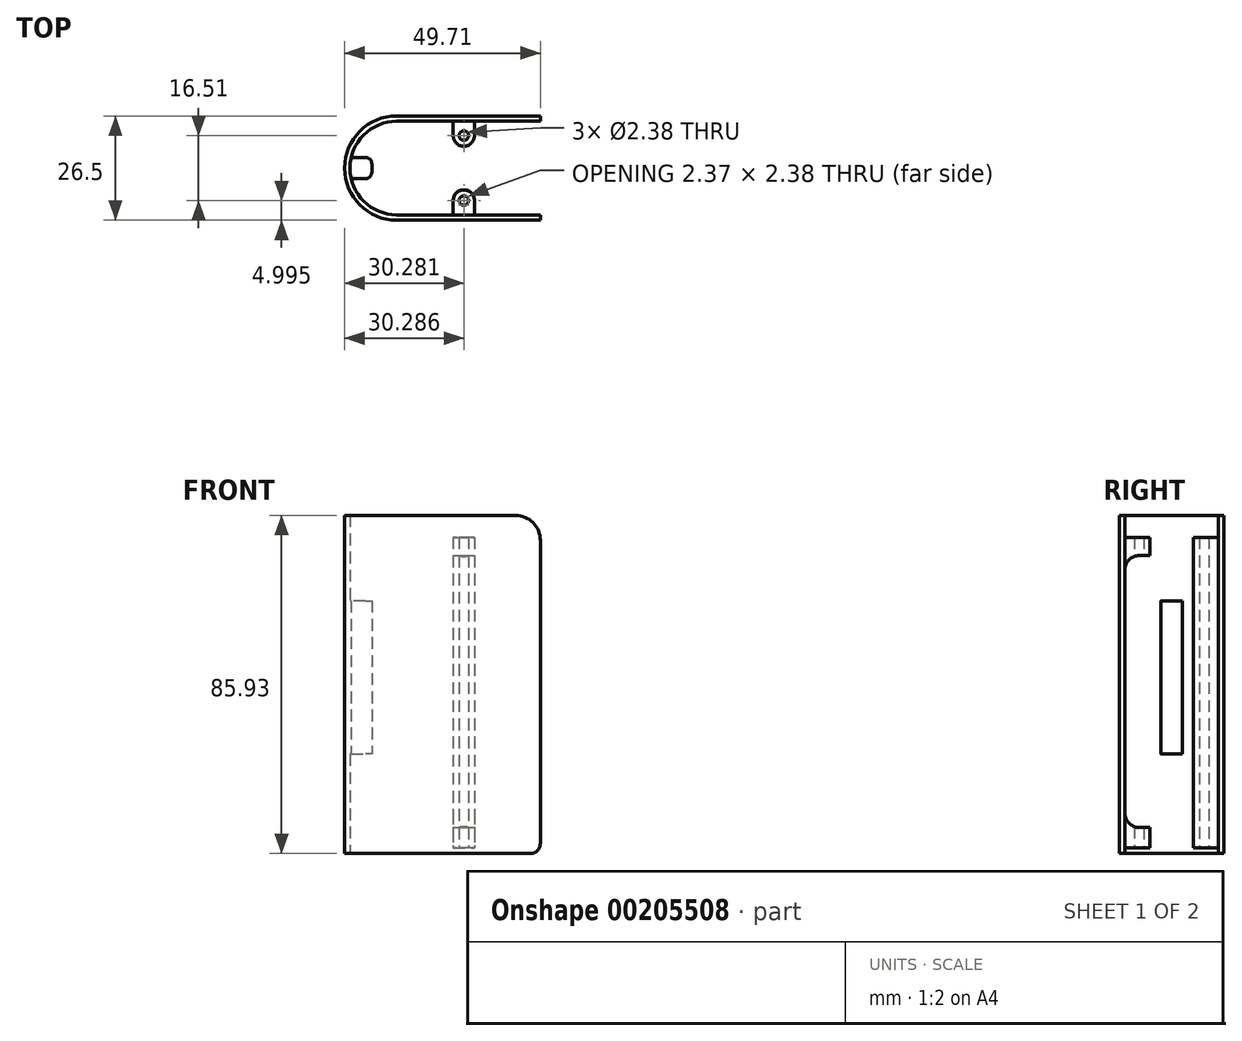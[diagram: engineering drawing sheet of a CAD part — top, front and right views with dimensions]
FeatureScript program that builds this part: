
annotation { "Feature Type Name" : "Feature", "Feature Type Description" : "" }
export const myFeature = defineFeature(function(context is Context, id is Id, definition is map)
    precondition{}
    {
        {
            var Q0;
            Q0=qCreatedBy(makeId("Top.planeOp"),FACE);
            var sketch = newSketch(context, id + "F0", { "sketchPlane" : qUnion([Q0])});
            skArc(sketch, "E0", {"start": v(0, 13.25) * mm, "mid": v(-9.37, 9.37) * mm, "end": v(-13.25, 0) * mm});
            skLineSegment(sketch, "E1", {"start": v(36.46, 13.25) * mm, "end": v(0, 13.25) * mm});
            skLineSegment(sketch, "E2", {"start": v(36.46, 11.9) * mm, "end": v(19.74, 11.9) * mm});
            skArc(sketch, "E3", {"start": v(0, 11.9) * mm, "mid": v(-7.4, 9.32) * mm, "end": v(-11.59, 2.7) * mm});
            skLineSegment(sketch, "E4.trimOffspring", {"start": v(36.46, 11.9) * mm, "end": v(36.46, 13.25) * mm});
            skLineSegment(sketch, "E5", {"start": v(14.33, 8.25) * mm, "end": v(14.33, 11.9) * mm});
            skLineSegment(sketch, "E6.trimOffspring", {"start": v(14.33, 11.9) * mm, "end": v(0, 11.9) * mm});
            skArc(sketch, "E7", {"start": v(14.33, 8.25) * mm, "mid": v(17.03, 5.55) * mm, "end": v(19.74, 8.25) * mm});
            skLineSegment(sketch, "E8.trimOffspring", {"start": v(19.74, 8.25) * mm, "end": v(19.74, 11.9) * mm});
            skCircle(sketch, "E9", {"center": v(17.03, 8.25) * mm, "radius": 1.2 * mm});
            skArc(sketch, "E10.MirrorCS", {"start": v(0, -11.9) * mm, "mid": v(-7.4, -9.32) * mm, "end": v(-11.59, -2.7) * mm});
            skArc(sketch, "E11.MirrorCS", {"start": v(0, -13.25) * mm, "mid": v(-9.37, -9.37) * mm, "end": v(-13.25, 0) * mm});
            skLineSegment(sketch, "E12.MirrorCS", {"start": v(14.33, -11.9) * mm, "end": v(0, -11.9) * mm});
            skLineSegment(sketch, "E13.MirrorCS", {"start": v(36.46, -13.25) * mm, "end": v(0, -13.25) * mm});
            skLineSegment(sketch, "E14.MirrorCS", {"start": v(14.33, -8.25) * mm, "end": v(14.33, -11.9) * mm});
            skArc(sketch, "E15.MirrorCS", {"start": v(14.33, -8.25) * mm, "mid": v(17.03, -5.55) * mm, "end": v(19.74, -8.25) * mm});
            skCircle(sketch, "E16.MirrorC", {"center": v(17.03, -8.25) * mm, "radius": 1.2 * mm});
            skLineSegment(sketch, "E17.MirrorCS", {"start": v(19.74, -8.25) * mm, "end": v(19.74, -11.9) * mm});
            skLineSegment(sketch, "E18.MirrorCS", {"start": v(36.46, -11.9) * mm, "end": v(19.74, -11.9) * mm});
            skLineSegment(sketch, "E19.MirrorCS", {"start": v(36.46, -11.9) * mm, "end": v(36.46, -13.25) * mm});
            skLineSegment(sketch, "E20.bottom", {"start": v(-7.99, 2.7) * mm, "end": v(-11.59, 2.7) * mm});
            skLineSegment(sketch, "E20.top", {"start": v(-7.99, -2.7) * mm, "end": v(-11.59, -2.7) * mm});
            skLineSegment(sketch, "E20.left", {"start": v(-6.34, 1.05) * mm, "end": v(-6.34, -1.05) * mm});
            skPoint(sketch, "E20.middle", {"position": v(-11.9, 0) * mm});
            skPoint(sketch, "E21.visualSharp", {"position": v(-6.34, 2.7) * mm});
            skArc(sketch, "E21.filletArc", {"start": v(-6.34, 1.05) * mm, "mid": v(-6.82, 2.22) * mm, "end": v(-7.99, 2.7) * mm});
            skPoint(sketch, "E22.visualSharp", {"position": v(-6.34, -2.7) * mm});
            skArc(sketch, "E22.filletArc", {"start": v(-7.99, -2.7) * mm, "mid": v(-6.82, -2.22) * mm, "end": v(-6.34, -1.05) * mm});
            skSolve(sketch);
        }
        {
            var Q0;
            Q0 = qSketchRegion(id + "F0", true);
            extrude(context, id + "F1", {"entities" : qUnion([Q0]), "depth" : 85.93 * mm});
        }
        {
            var Q0;
            Q0=makeQuery(id+"F1.opExtrude","CAP_FACE",FACE,{"disambiguationData":[OSD([sQuery(id+"F0.wireOp",EDGE,"E0"),sQuery(id+"F0.wireOp",EDGE,"E1"),sQuery(id+"F0.wireOp",EDGE,"E2"),sQuery(id+"F0.wireOp",EDGE,"E3"),sQuery(id+"F0.wireOp",EDGE,"E4.trimOffspring"),sQuery(id+"F0.wireOp",EDGE,"E5"),sQuery(id+"F0.wireOp",EDGE,"E6.trimOffspring"),sQuery(id+"F0.wireOp",EDGE,"E7"),sQuery(id+"F0.wireOp",EDGE,"E8.trimOffspring"),sQuery(id+"F0.wireOp",EDGE,"E9"),sQuery(id+"F0.wireOp",EDGE,"E10.MirrorCS"),sQuery(id+"F0.wireOp",EDGE,"E11.MirrorCS"),sQuery(id+"F0.wireOp",EDGE,"E12.MirrorCS"),sQuery(id+"F0.wireOp",EDGE,"E13.MirrorCS"),sQuery(id+"F0.wireOp",EDGE,"E14.MirrorCS"),sQuery(id+"F0.wireOp",EDGE,"E15.MirrorCS"),sQuery(id+"F0.wireOp",EDGE,"E16.MirrorC"),sQuery(id+"F0.wireOp",EDGE,"E17.MirrorCS"),sQuery(id+"F0.wireOp",EDGE,"E18.MirrorCS"),sQuery(id+"F0.wireOp",EDGE,"E19.MirrorCS"),sQuery(id+"F0.wireOp",EDGE,"E20.bottom"),sQuery(id+"F0.wireOp",EDGE,"E20.top"),sQuery(id+"F0.wireOp",EDGE,"E20.left"),sQuery(id+"F0.wireOp",EDGE,"E21.filletArc"),sQuery(id+"F0.wireOp",EDGE,"E22.filletArc")])],"isStart":false});
            var sketch = newSketch(context, id + "F2", { "sketchPlane" : qUnion([Q0])});
            skCircle(sketch, "E23", {"center": v(0, 0) * mm, "radius": 11.9 * mm});
            skLineSegment(sketch, "E24.bottom", {"start": v(14.33, 11.9) * mm, "end": v(19.74, 11.9) * mm});
            skLineSegment(sketch, "E24.top", {"start": v(14.33, -11.9) * mm, "end": v(19.74, -11.9) * mm});
            skLineSegment(sketch, "E24.left", {"start": v(14.33, 11.9) * mm, "end": v(14.33, -11.9) * mm});
            skLineSegment(sketch, "E24.right", {"start": v(19.74, 11.9) * mm, "end": v(19.74, -11.9) * mm});
            skSolve(sketch);
        }
        {
            var Q0;
            {var subQ2=makeQuery(id+"F1.opExtrude","CAP_EDGE",EDGE,{"disambiguationData":[OSD([sQuery(id+"F0.wireOp",EDGE,"E20.bottom")])],"isStart":false});Q0=makeQuery(id+"F2.imprint","IMPRINT",FACE,{"disambiguationData":[TD([[makeQuery(id+"F2.imprint","IMPRINT",EDGE,{"derivedFrom":subQ2}),1.0]])]});}
            extrude(context, id + "F3", {"entities" : qUnion([Q0]), "operationType" : NewBodyOperationType.REMOVE, "oppositeDirection" : true, "depth" : 21.72 * mm});
        }
        {
            var Q0;
            Q0 = qSketchRegion(id + "F2", true);
            extrude(context, id + "F4", {"entities" : qUnion([Q0]), "operationType" : NewBodyOperationType.REMOVE, "oppositeDirection" : true, "depth" : 5.6 * mm});
        }
        {
            var Q0;
            Q0=makeQuery(id+"F1.opExtrude","SWEPT_FACE",FACE,{"disambiguationData":[OSD([sQuery(id+"F0.wireOp",EDGE,"E17.MirrorCS")])]});
            var sketch = newSketch(context, id + "F5", { "sketchPlane" : qUnion([Q0])});
            skLineSegment(sketch, "E25", {"start": v(-11.9, 80.34) * mm, "end": v(-11.9, 75.77) * mm});
            skLineSegment(sketch, "E26", {"start": v(-8.25, 0) * mm, "end": v(-8.25, 6.6) * mm});
            skLineSegment(sketch, "E27.bottom", {"start": v(-8.25, 75.77) * mm, "end": v(-8.09, 75.77) * mm});
            skLineSegment(sketch, "E27.top", {"start": v(-8.25, 6.6) * mm, "end": v(-8.09, 6.6) * mm});
            skLineSegment(sketch, "E27.left", {"start": v(-11.9, 71.96) * mm, "end": v(-11.9, 10.41) * mm});
            skLineSegment(sketch, "E28.bottom", {"start": v(-8.25, 6.6) * mm, "end": v(-4.6, 6.6) * mm});
            skLineSegment(sketch, "E28.top", {"start": v(-8.25, 75.77) * mm, "end": v(-4.6, 75.77) * mm});
            skLineSegment(sketch, "E28.right", {"start": v(-4.6, 6.6) * mm, "end": v(-4.6, 75.77) * mm});
            skPoint(sketch, "E29.visualSharp", {"position": v(-11.9, 75.77) * mm});
            skArc(sketch, "E29.filletArc", {"start": v(-8.09, 75.77) * mm, "mid": v(-10.78, 74.65) * mm, "end": v(-11.9, 71.96) * mm});
            skPoint(sketch, "E30.visualSharp", {"position": v(-11.9, 6.6) * mm});
            skArc(sketch, "E30.filletArc", {"start": v(-11.9, 10.41) * mm, "mid": v(-10.78, 7.72) * mm, "end": v(-8.09, 6.6) * mm});
            skLineSegment(sketch, "E31.MirrorCS", {"start": v(8.25, 6.6) * mm, "end": v(8.09, 6.6) * mm});
            skLineSegment(sketch, "E32.MirrorCS", {"start": v(8.25, 75.77) * mm, "end": v(8.09, 75.77) * mm});
            skArc(sketch, "E33.MirrorCS", {"start": v(11.9, 10.41) * mm, "mid": v(10.78, 7.72) * mm, "end": v(8.09, 6.6) * mm});
            skArc(sketch, "E34.MirrorCS", {"start": v(8.09, 75.77) * mm, "mid": v(10.78, 74.65) * mm, "end": v(11.9, 71.96) * mm});
            skLineSegment(sketch, "E35.MirrorCS", {"start": v(8.25, 75.77) * mm, "end": v(4.6, 75.77) * mm});
            skLineSegment(sketch, "E36.MirrorCS", {"start": v(8.25, 6.6) * mm, "end": v(4.6, 6.6) * mm});
            skLineSegment(sketch, "E37.MirrorCS", {"start": v(11.9, 80.34) * mm, "end": v(11.9, 75.77) * mm});
            skLineSegment(sketch, "E38.MirrorCS", {"start": v(8.25, 0) * mm, "end": v(8.25, 6.6) * mm});
            skPoint(sketch, "E39.MirrorP", {"position": v(11.9, 6.6) * mm});
            skPoint(sketch, "E40.MirrorP", {"position": v(11.9, 75.77) * mm});
            skLineSegment(sketch, "E41.MirrorCS", {"start": v(4.6, 6.6) * mm, "end": v(4.6, 75.77) * mm});
            skLineSegment(sketch, "E42.MirrorCS", {"start": v(11.9, 71.96) * mm, "end": v(11.9, 10.41) * mm});
            skSolve(sketch);
        }
        {
            var Q0;
            {var subQ0=sQuery(id+"F5.wireOp",EDGE,"E27.left");Q0=makeQuery(id+"F5.imprint","IMPRINT",FACE,{"disambiguationData":[TD([[makeQuery(id+"F5.imprint","IMPRINT",EDGE,{"derivedFrom":subQ0}),1.0]])]});}
            var Q1;
            {var subQ5=sQuery(id+"F5.wireOp",EDGE,"E28.right");Q1=makeQuery(id+"F5.imprint","IMPRINT",FACE,{"disambiguationData":[TD([[makeQuery(id+"F5.imprint","IMPRINT",EDGE,{"derivedFrom":subQ5}),1.0]])]});}
            var Q2;
            {var subQ1=sQuery(id+"F5.wireOp",EDGE,"E33.MirrorCS");Q2=makeQuery(id+"F5.imprint","IMPRINT",FACE,{"disambiguationData":[TD([[makeQuery(id+"F5.imprint","IMPRINT",EDGE,{"derivedFrom":subQ1}),-1.0]])]});}
            extrude(context, id + "F6", {"entities" : qUnion([Q0, Q1, Q2]), "operationType" : NewBodyOperationType.REMOVE, "oppositeDirection" : true, "depth" : 6.35 * mm});
        }
        {
            var Q0;
            {var subQ3=sQuery(id+"F0.wireOp",EDGE,"E8.trimOffspring");Q0=makeQuery(id+"F6.boolean.opBoolean","SPLIT",FACE,{"disambiguationData":[TD([makeQuery(id+"F6.opExtrude","SWEPT_FACE",FACE,{"disambiguationData":[OSD([sQuery(id+"F5.wireOp",EDGE,"E33.MirrorCS")])]})])],"derivedFrom":makeQuery(id+"F1.opExtrude","SWEPT_FACE",FACE,{"disambiguationData":[OSD([subQ3])]})});}
            var sketch = newSketch(context, id + "F7", { "sketchPlane" : qUnion([Q0])});
            skLineSegment(sketch, "E43.bottom", {"start": v(11.9, 1.4) * mm, "end": v(-11.9, 1.4) * mm});
            skLineSegment(sketch, "E43.top", {"start": v(11.9, -1.4) * mm, "end": v(-11.9, -1.4) * mm});
            skLineSegment(sketch, "E43.left", {"start": v(11.9, 1.4) * mm, "end": v(11.9, -1.4) * mm});
            skLineSegment(sketch, "E43.right", {"start": v(-11.9, 1.4) * mm, "end": v(-11.9, -1.4) * mm});
            skPoint(sketch, "E43.middle", {"position": v(0, 0) * mm});
            skSolve(sketch);
        }
        {
            var Q0;
            {var subQ3=sQuery(id+"F7.wireOp",EDGE,"E43.top");Q0=makeQuery(id+"F7.imprint","IMPRINT",FACE,{"disambiguationData":[TD([[makeQuery(id+"F7.imprint","IMPRINT",EDGE,{"derivedFrom":subQ3}),-1.0]])]});}
            var Q1;
            {var subQ2=sQuery(id+"F0.wireOp",EDGE,"E8.trimOffspring");var subQ12=makeQuery(id+"F1.opExtrude","CAP_EDGE",EDGE,{"disambiguationData":[OSD([subQ2])],"isStart":true});Q1=makeQuery(id+"F7.imprint","IMPRINT",FACE,{"disambiguationData":[TD([[makeQuery(id+"F7.imprint","IMPRINT",EDGE,{"derivedFrom":subQ12}),1.0]])]});}
            extrude(context, id + "F8", {"entities" : qUnion([Q0, Q1]), "operationType" : NewBodyOperationType.REMOVE, "oppositeDirection" : true, "depth" : 6.35 * mm});
        }
        {
            var Q0;
            Q0=makeQuery(id+"F1.opExtrude","CAP_FACE",FACE,{"disambiguationData":[OSD([sQuery(id+"F0.wireOp",EDGE,"E0"),sQuery(id+"F0.wireOp",EDGE,"E1"),sQuery(id+"F0.wireOp",EDGE,"E2"),sQuery(id+"F0.wireOp",EDGE,"E3"),sQuery(id+"F0.wireOp",EDGE,"E4.trimOffspring"),sQuery(id+"F0.wireOp",EDGE,"E5"),sQuery(id+"F0.wireOp",EDGE,"E6.trimOffspring"),sQuery(id+"F0.wireOp",EDGE,"E7"),sQuery(id+"F0.wireOp",EDGE,"E8.trimOffspring"),sQuery(id+"F0.wireOp",EDGE,"E9"),sQuery(id+"F0.wireOp",EDGE,"E10.MirrorCS"),sQuery(id+"F0.wireOp",EDGE,"E11.MirrorCS"),sQuery(id+"F0.wireOp",EDGE,"E12.MirrorCS"),sQuery(id+"F0.wireOp",EDGE,"E13.MirrorCS"),sQuery(id+"F0.wireOp",EDGE,"E14.MirrorCS"),sQuery(id+"F0.wireOp",EDGE,"E15.MirrorCS"),sQuery(id+"F0.wireOp",EDGE,"E16.MirrorC"),sQuery(id+"F0.wireOp",EDGE,"E17.MirrorCS"),sQuery(id+"F0.wireOp",EDGE,"E18.MirrorCS"),sQuery(id+"F0.wireOp",EDGE,"E19.MirrorCS"),sQuery(id+"F0.wireOp",EDGE,"E20.bottom"),sQuery(id+"F0.wireOp",EDGE,"E20.top"),sQuery(id+"F0.wireOp",EDGE,"E20.left"),sQuery(id+"F0.wireOp",EDGE,"E21.filletArc"),sQuery(id+"F0.wireOp",EDGE,"E22.filletArc")])],"isStart":true});
            var sketch = newSketch(context, id + "F9", { "sketchPlane" : qUnion([Q0])});
            skCircle(sketch, "E44", {"center": v(0, 0) * mm, "radius": 11.9 * mm});
            skSolve(sketch);
        }
        {
            var Q0;
            Q0 = qSketchRegion(id + "F9", true);
            extrude(context, id + "F10", {"entities" : qUnion([Q0]), "operationType" : NewBodyOperationType.REMOVE, "oppositeDirection" : true, "depth" : 25.27 * mm});
        }
        {
            var Q0;
            Q0=makeQuery(id+"F1.opExtrude","SWEPT_FACE",FACE,{"disambiguationData":[OSD([sQuery(id+"F0.wireOp",EDGE,"E13.MirrorCS")])]});
            var sketch = newSketch(context, id + "F11", { "sketchPlane" : qUnion([Q0])});
            skPoint(sketch, "E45.visualSharp", {"position": v(36.46, 0) * mm});
            skArc(sketch, "E45.filletArc", {"start": v(33.92, 0) * mm, "mid": v(35.72, 0.74) * mm, "end": v(36.46, 2.54) * mm});
            skPoint(sketch, "E46.visualSharp", {"position": v(36.46, 85.93) * mm});
            skArc(sketch, "E46.filletArc", {"start": v(36.46, 79.58) * mm, "mid": v(34.6, 84.07) * mm, "end": v(30.11, 85.93) * mm});
            skSolve(sketch);
        }
        {
            var Q0;
            {var subQ0=sQuery(id+"F11.wireOp",EDGE,"E46.filletArc");Q0=makeQuery(id+"F11.imprint","IMPRINT",FACE,{"disambiguationData":[TD([[makeQuery(id+"F11.imprint","IMPRINT",EDGE,{"derivedFrom":subQ0}),-1.0]])]});}
            var Q1;
            {var subQ0=sQuery(id+"F11.wireOp",EDGE,"E45.filletArc");Q1=makeQuery(id+"F11.imprint","IMPRINT",FACE,{"disambiguationData":[TD([[makeQuery(id+"F11.imprint","IMPRINT",EDGE,{"derivedFrom":subQ0}),-1.0]])]});}
            var Q2;
            Q2=makeQuery(id+"F1.opExtrude","SWEPT_FACE",FACE,{"disambiguationData":[OSD([sQuery(id+"F0.wireOp",EDGE,"E1")])]});
            extrude(context, id + "F12", {"entities" : qUnion([Q0, Q1]), "operationType" : NewBodyOperationType.REMOVE, "endBound" : BoundingType.UP_TO_SURFACE, "oppositeDirection" : true, "endBoundEntityFace" : qUnion([Q2]), "depth" : 25.4 * mm});
        }
    });
